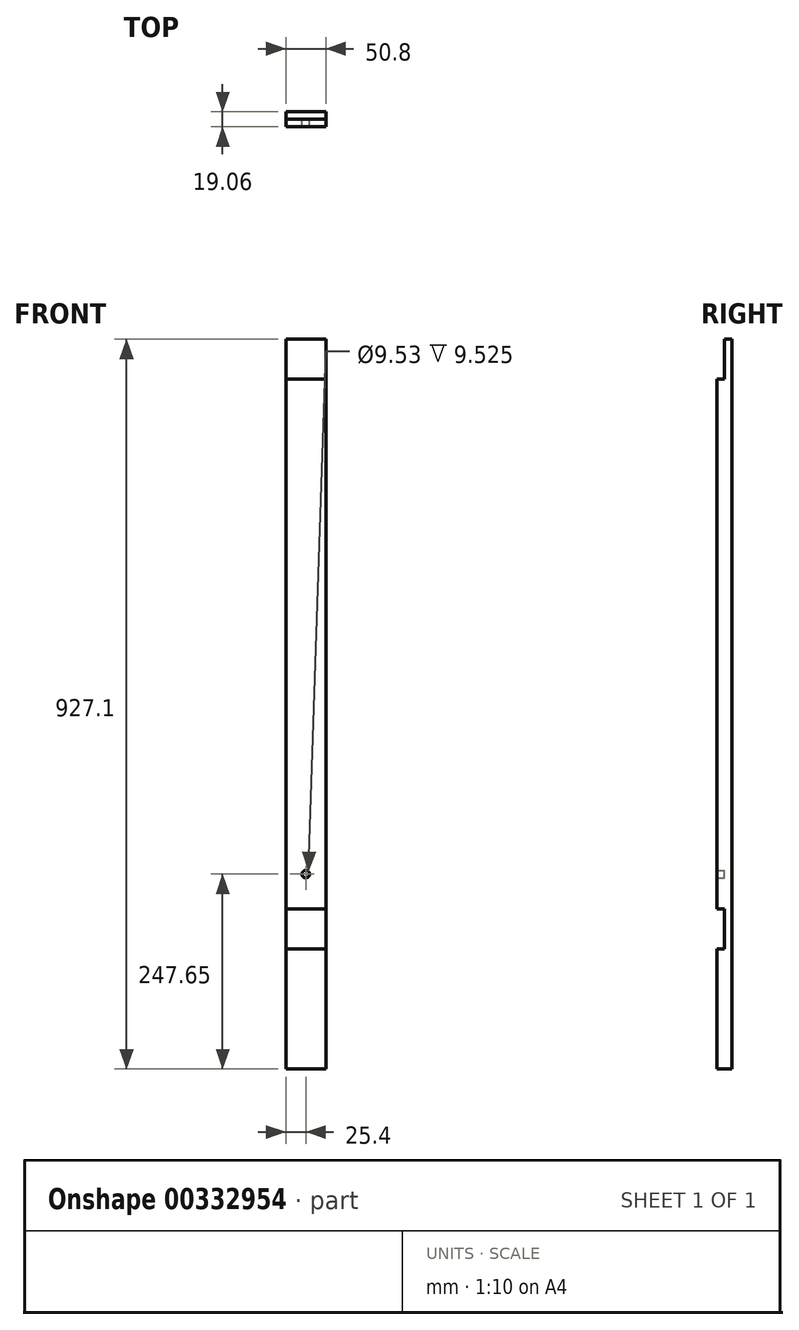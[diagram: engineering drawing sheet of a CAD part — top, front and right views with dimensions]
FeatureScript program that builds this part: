
annotation { "Feature Type Name" : "Feature", "Feature Type Description" : "" }
export const myFeature = defineFeature(function(context is Context, id is Id, definition is map)
    precondition{}
    {
        {
            var Q0;
            Q0=qCreatedBy(makeId("Top.planeOp"),FACE);
            var sketch = newSketch(context, id + "F0", { "sketchPlane" : qUnion([Q0])});
            skLineSegment(sketch, "E0.bottom", {"start": v(25.4, 9.53) * mm, "end": v(-25.4, 9.53) * mm});
            skLineSegment(sketch, "E0.top", {"start": v(25.4, -9.53) * mm, "end": v(-25.4, -9.53) * mm});
            skLineSegment(sketch, "E0.left", {"start": v(25.4, 9.53) * mm, "end": v(25.4, -9.52) * mm});
            skLineSegment(sketch, "E0.right", {"start": v(-25.4, 9.53) * mm, "end": v(-25.4, -9.53) * mm});
            skPoint(sketch, "E0.middle", {"position": v(0, 0) * mm});
            skSolve(sketch);
        }
        {
            var Q0;
            Q0=makeQuery(id+"F0.imprint","IMPRINT",FACE,{"disambiguationData":[TD([[makeQuery(id+"F0.imprint","IMPRINT",EDGE,{"derivedFrom":sQuery(id+"F0.wireOp",EDGE,"E0.bottom")}),1.0]])]});
            var Q1;
            Q1=qSketchRegion(id+"F2",true);
            extrude(context, id + "F1", {"entities" : qUnion([Q0, Q1]), "depth" : 927.1 * mm});
        }
        {
            var Q0;
            Q0=qCreatedBy(makeId("Front.planeOp"),FACE);
            var sketch = newSketch(context, id + "F2", { "sketchPlane" : qUnion([Q0])});
            skLineSegment(sketch, "E1.bottom", {"start": v(-38.77, 152.4) * mm, "end": v(83.66, 152.4) * mm});
            skLineSegment(sketch, "E1.top", {"start": v(-38.77, 203.2) * mm, "end": v(83.66, 203.2) * mm});
            skLineSegment(sketch, "E1.left", {"start": v(-38.77, 152.4) * mm, "end": v(-38.77, 203.2) * mm});
            skLineSegment(sketch, "E1.right", {"start": v(83.66, 152.4) * mm, "end": v(83.66, 203.2) * mm});
            skLineSegment(sketch, "E2.bottom", {"start": v(-210.36, 876.3) * mm, "end": v(132.8, 876.3) * mm});
            skLineSegment(sketch, "E2.top", {"start": v(-210.36, 927.1) * mm, "end": v(132.8, 927.1) * mm});
            skLineSegment(sketch, "E2.left", {"start": v(-210.36, 876.3) * mm, "end": v(-210.36, 927.1) * mm});
            skLineSegment(sketch, "E2.right", {"start": v(132.8, 876.3) * mm, "end": v(132.8, 927.1) * mm});
            skSolve(sketch);
        }
        {
            var Q0;
            Q0=qSketchRegion(id+"F2",true);
            extrude(context, id + "F3", {"entities" : qUnion([Q0]), "operationType" : NewBodyOperationType.REMOVE, "depth" : 25.4 * mm});
        }
        {
            var Q0;
            Q0=qCreatedBy(makeId("Front.planeOp"),FACE);
            var sketch = newSketch(context, id + "F4", { "sketchPlane" : qUnion([Q0])});
            skCircle(sketch, "E3", {"center": v(0, 247.65) * mm, "radius": 4.76 * mm});
            skSolve(sketch);
        }
        {
            var Q0;
            Q0=qSketchRegion(id+"F4",true);
            extrude(context, id + "F5", {"entities" : qUnion([Q0]), "operationType" : NewBodyOperationType.REMOVE, "depth" : 25.4 * mm});
        }
    });
